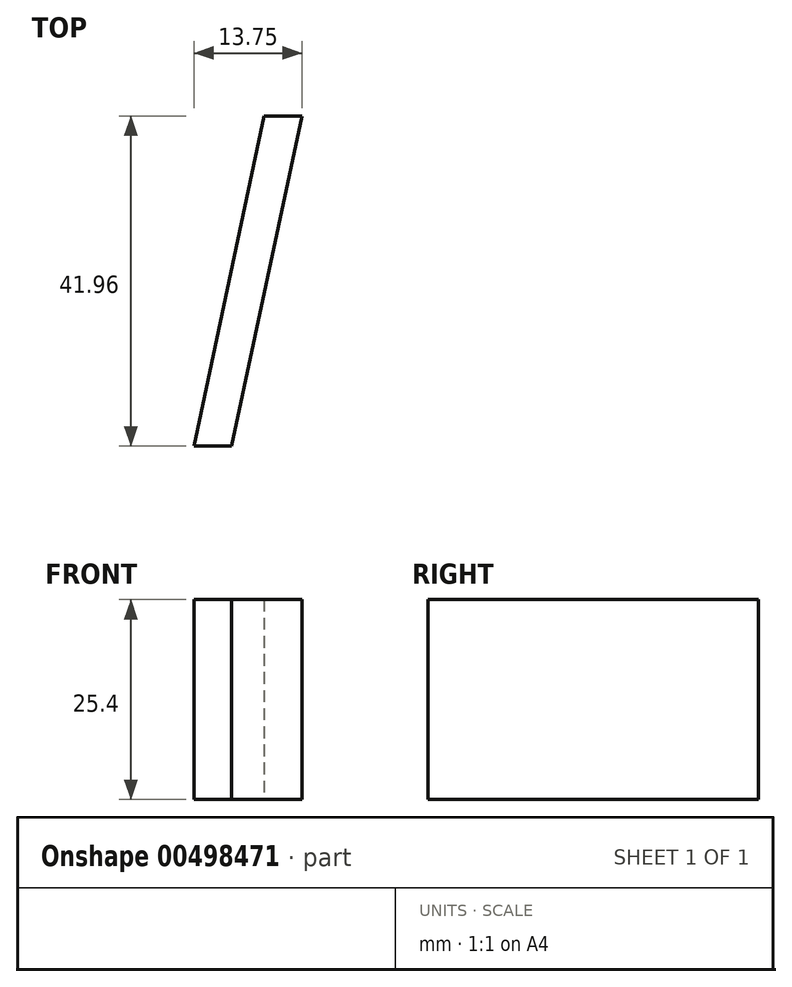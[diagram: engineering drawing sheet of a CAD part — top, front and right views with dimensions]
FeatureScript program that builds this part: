
annotation { "Feature Type Name" : "Feature", "Feature Type Description" : "" }
export const myFeature = defineFeature(function(context is Context, id is Id, definition is map)
    precondition{}
    {
        {
            var Q0;
            Q0=qCreatedBy(makeId("Top.planeOp"),FACE);
            var sketch = newSketch(context, id + "F0", { "sketchPlane" : qUnion([Q0])});
            skText(sketch, "E0", { "text": "RISE UP", "fontName": "OpenSans-Italic.ttf"});
            const initialGuessF0  = {"E0": [0, -0.04232, 1, 0, 0.04232]};
            skSetInitialGuess(sketch, initialGuessF0);
            skSolve(sketch);
        }
        {
            var Q0;
            Q0 = qSketchRegion(id + "F0", true);
            var sketch = newSketch(context, id + "F1", { "sketchPlane" : qUnion([Q0])});
            skSolve(sketch);
        }
        {
            var Q0;
            Q0 = qSketchRegion(id + "F1", true);
            var Q1;
            Q1=makeQuery(id+"F1.imprint","IMPRINT",FACE,{"disambiguationData":[TD([[makeQuery(id+"F1.imprint","IMPRINT",EDGE,{"derivedFrom":makeQuery(id+"F0.imprint","IMPRINT",EDGE,{"derivedFrom":sQuery(id+"F0.wireOp",EDGE,"E0.sketch_text.stroke-48")})}),-1.0]])]});
            var Q2;
            Q2=makeQuery(id+"F1.imprint","IMPRINT",FACE,{"disambiguationData":[TD([[makeQuery(id+"F1.imprint","IMPRINT",EDGE,{"derivedFrom":makeQuery(id+"F0.imprint","IMPRINT",EDGE,{"derivedFrom":sQuery(id+"F0.wireOp",EDGE,"E0.sketch_text.stroke-21")})}),-1.0]])]});
            var Q3;
            Q3=makeQuery(id+"F1.imprint","IMPRINT",FACE,{"disambiguationData":[TD([[makeQuery(id+"F1.imprint","IMPRINT",EDGE,{"derivedFrom":makeQuery(id+"F0.imprint","IMPRINT",EDGE,{"derivedFrom":sQuery(id+"F0.wireOp",EDGE,"E0.sketch_text.stroke-17")})}),-1.0]])]});
            var Q4;
            Q4=makeQuery(id+"F1.imprint","IMPRINT",FACE,{"disambiguationData":[TD([[makeQuery(id+"F1.imprint","IMPRINT",EDGE,{"derivedFrom":makeQuery(id+"F0.imprint","IMPRINT",EDGE,{"derivedFrom":sQuery(id+"F0.wireOp",EDGE,"E0.sketch_text.stroke-60")})}),-1.0]])]});
            var Q5;
            Q5=makeQuery(id+"F1.imprint","IMPRINT",FACE,{"disambiguationData":[TD([[makeQuery(id+"F1.imprint","IMPRINT",EDGE,{"derivedFrom":makeQuery(id+"F0.imprint","IMPRINT",EDGE,{"derivedFrom":sQuery(id+"F0.wireOp",EDGE,"E0.sketch_text.stroke-0")})}),-1.0]])]});
            var Q6;
            Q6=makeQuery(id+"F1.imprint","IMPRINT",FACE,{"disambiguationData":[TD([[makeQuery(id+"F1.imprint","IMPRINT",EDGE,{"derivedFrom":makeQuery(id+"F0.imprint","IMPRINT",EDGE,{"derivedFrom":sQuery(id+"F0.wireOp",EDGE,"E0.sketch_text.stroke-76")})}),-1.0]])]});
            extrude(context, id + "F2", {"entities" : qUnion([Q0, Q1, Q2, Q3, Q4, Q5, Q6]), "depth" : 25.4 * mm});
        }
    });
